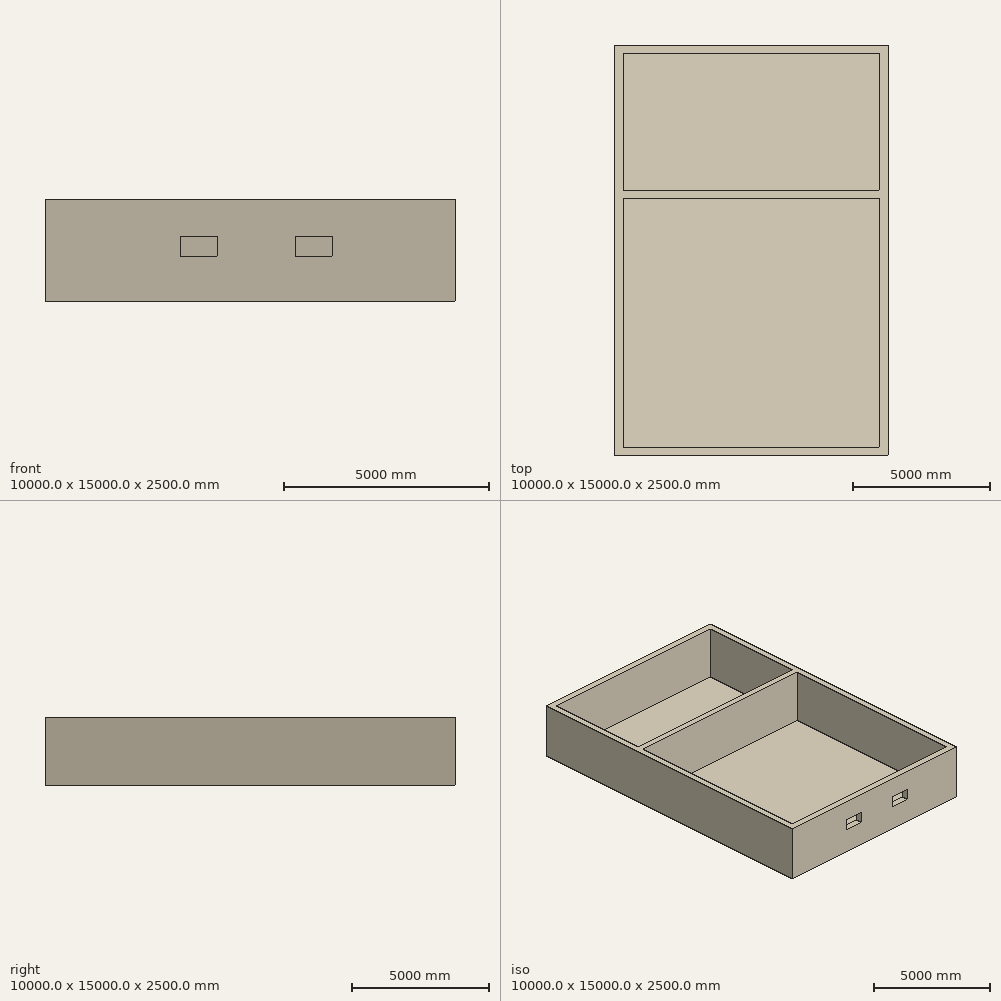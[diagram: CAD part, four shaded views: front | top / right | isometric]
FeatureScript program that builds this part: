
annotation { "Feature Type Name" : "Feature", "Feature Type Description" : "" }
export const myFeature = defineFeature(function(context is Context, id is Id, definition is map)
    precondition{}
    {
        {
            var Q0;
            Q0=qCreatedBy(makeId("Top.planeOp"),FACE);
            var sketch = newSketch(context, id + "F0", { "sketchPlane" : qUnion([Q0])});
            skLineSegment(sketch, "E0.bottom", {"start": v(-6139.29, 81.94) * mm, "end": v(3860.71, 81.94) * mm});
            skLineSegment(sketch, "E0.top", {"start": v(-6139.29, -14918.06) * mm, "end": v(3860.71, -14918.06) * mm});
            skLineSegment(sketch, "E0.left", {"start": v(-6139.29, 81.94) * mm, "end": v(-6139.29, -14918.06) * mm});
            skLineSegment(sketch, "E0.right", {"start": v(3860.71, 81.94) * mm, "end": v(3860.71, -14918.06) * mm});
            skSolve(sketch);
        }
        {
            var Q0;
            Q0 = qSketchRegion(id + "F0", true);
            extrude(context, id + "F1", {"entities" : qUnion([Q0]), "depth" : 100 * mm, "offsetDistance" : 25 * mm});
        }
        {
            var Q0;
            Q0=makeQuery(id+"F1.opExtrude","CAP_FACE",FACE,{"disambiguationData":[OSD([sQuery(id+"F0.wireOp",EDGE,"E0.bottom"),sQuery(id+"F0.wireOp",EDGE,"E0.top"),sQuery(id+"F0.wireOp",EDGE,"E0.left"),sQuery(id+"F0.wireOp",EDGE,"E0.right")])],"isStart":false});
            var sketch = newSketch(context, id + "F2", { "sketchPlane" : qUnion([Q0])});
            skLineSegment(sketch, "E1.0", {"start": v(-5839.29, -218.06) * mm, "end": v(-5839.29, -5218.06) * mm});
            skLineSegment(sketch, "E1.1", {"start": v(3560.71, -218.06) * mm, "end": v(-5839.29, -218.06) * mm});
            skLineSegment(sketch, "E1.2", {"start": v(3560.71, -14618.06) * mm, "end": v(3560.71, -5518.06) * mm});
            skLineSegment(sketch, "E1.3", {"start": v(-5839.29, -14618.06) * mm, "end": v(3560.71, -14618.06) * mm});
            skLineSegment(sketch, "E2.0.0", {"start": v(-6139.29, 81.94) * mm, "end": v(-6139.29, -14918.06) * mm});
            skLineSegment(sketch, "E2.0.1", {"start": v(-6139.29, -14918.06) * mm, "end": v(3860.71, -14918.06) * mm});
            skLineSegment(sketch, "E2.0.2", {"start": v(3860.71, -14918.06) * mm, "end": v(3860.71, 81.94) * mm});
            skLineSegment(sketch, "E2.0.3", {"start": v(3860.71, 81.94) * mm, "end": v(-6139.29, 81.94) * mm});
            skLineSegment(sketch, "E3.bottom", {"start": v(-5839.29, -5218.06) * mm, "end": v(3560.71, -5218.06) * mm});
            skLineSegment(sketch, "E3.top", {"start": v(-5839.29, -5518.06) * mm, "end": v(3560.71, -5518.06) * mm});
            skLineSegment(sketch, "E4.trimOffspring", {"start": v(-5839.29, -5518.06) * mm, "end": v(-5839.29, -14618.06) * mm});
            skLineSegment(sketch, "E5.trimOffspring", {"start": v(3560.71, -5218.06) * mm, "end": v(3560.71, -218.06) * mm});
            skSolve(sketch);
        }
        {
            var Q0;
            Q0 = qSketchRegion(id + "F2", true);
            extrude(context, id + "F3", {"entities" : qUnion([Q0]), "operationType" : NewBodyOperationType.ADD, "depth" : 2400 * mm, "offsetDistance" : 25 * mm});
        }
        {
            var Q0;
            Q0=makeQuery(id+"F3.boolean.opBoolean","MERGE",FACE,{"derivedFrom":[makeQuery(id+"F1.opExtrude","SWEPT_FACE",FACE,{"disambiguationData":[OSD([sQuery(id+"F0.wireOp",EDGE,"E0.top")])]}),makeQuery(id+"F3.opExtrude","SWEPT_FACE",FACE,{"disambiguationData":[OSD([sQuery(id+"F2.wireOp",EDGE,"E2.0.1")])]})]});
            var sketch = newSketch(context, id + "F4", { "sketchPlane" : qUnion([Q0])});
            skLineSegment(sketch, "E6.bottom", {"start": v(-39.29, 1600) * mm, "end": v(860.71, 1600) * mm});
            skLineSegment(sketch, "E6.top", {"start": v(-39.29, 1100) * mm, "end": v(860.71, 1100) * mm});
            skLineSegment(sketch, "E6.left", {"start": v(-39.29, 1600) * mm, "end": v(-39.29, 1100) * mm});
            skLineSegment(sketch, "E6.right", {"start": v(860.71, 1600) * mm, "end": v(860.71, 1100) * mm});
            skLineSegment(sketch, "E7.1.0.0", {"start": v(-2839.29, 1100) * mm, "end": v(-1939.29, 1100) * mm});
            skLineSegment(sketch, "E7.1.0.1", {"start": v(-2839.29, 1600) * mm, "end": v(-1939.29, 1600) * mm});
            skLineSegment(sketch, "E7.1.0.2", {"start": v(-1939.29, 1600) * mm, "end": v(-1939.29, 1100) * mm});
            skLineSegment(sketch, "E7.1.0.3", {"start": v(-2839.29, 1600) * mm, "end": v(-2839.29, 1100) * mm});
            skLineSegment(sketch, "E7.direction1", {"start": v(-39.29, 1100) * mm, "end": v(-2839.29, 1100) * mm, "construction": true});
            skSolve(sketch);
        }
        {
            var Q0;
            Q0 = qSketchRegion(id + "F4", true);
            var Q1;
            Q1=makeQuery(id+"F3.opExtrude","SWEPT_FACE",FACE,{"disambiguationData":[OSD([sQuery(id+"F2.wireOp",EDGE,"E1.3")])]});
            extrude(context, id + "F5", {"entities" : qUnion([Q0]), "operationType" : NewBodyOperationType.REMOVE, "endBound" : BoundingType.UP_TO_SURFACE, "oppositeDirection" : true, "depth" : 25 * mm, "endBoundEntityFace" : qUnion([Q1]), "offsetDistance" : 25 * mm});
        }
    });
